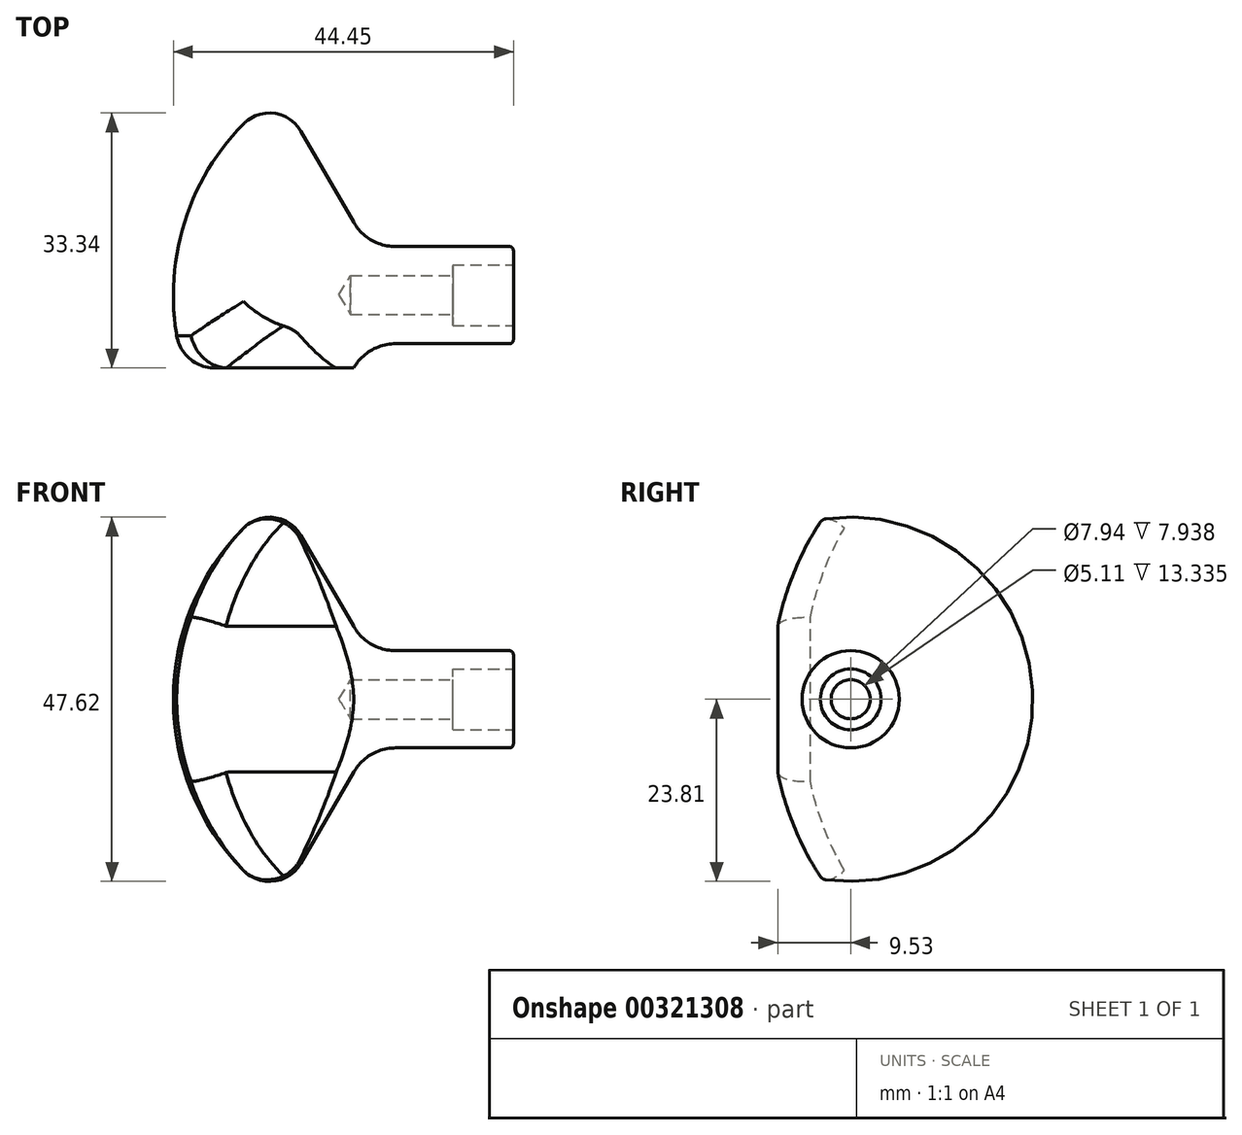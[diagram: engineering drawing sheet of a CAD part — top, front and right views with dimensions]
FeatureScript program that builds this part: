
annotation { "Feature Type Name" : "Feature", "Feature Type Description" : "" }
export const myFeature = defineFeature(function(context is Context, id is Id, definition is map)
    precondition{}
    {
        {
            var Q0;
            Q0=qCreatedBy(makeId("Top.planeOp"),FACE);
            var sketch = newSketch(context, id + "F0", { "sketchPlane" : qUnion([Q0])});
            skLineSegment(sketch, "E0", {"start": v(0, 0) * mm, "end": v(-44.45, 0) * mm});
            skLineSegment(sketch, "E1", {"start": v(0, 0) * mm, "end": v(0, 6.35) * mm});
            skLineSegment(sketch, "E2", {"start": v(0, 6.35) * mm, "end": v(-19.05, 6.35) * mm});
            skLineSegment(sketch, "E3", {"start": v(-19.05, 6.35) * mm, "end": v(-27.76, 21.43) * mm});
            skArc(sketch, "E4", {"start": v(-27.76, 21.43) * mm, "mid": v(-31.28, 23.77) * mm, "end": v(-35.27, 22.4) * mm});
            skLineSegment(sketch, "E5", {"start": v(0, 0) * mm, "end": v(5.66, 0) * mm, "construction": true});
            skArc(sketch, "E6", {"start": v(-35.27, 22.4) * mm, "mid": v(-42.07, 12.1) * mm, "end": v(-44.45, 0) * mm});
            skSolve(sketch);
        }
        {
            var Q0;
            Q0 = qSketchRegion(id + "F0", true);
            var Q1;
            Q1=sQuery(id+"F0.wireOp",EDGE,"E0");
            revolve(context, id + "F1", {"entities" : qUnion([Q0]), "axis" : qUnion([Q1]), "revolveType" : RevolveType.FULL});
        }
        {
            var Q0;
            Q0=makeQuery(id+"F1.opRevolve","SWEPT_FACE",FACE,{"disambiguationData":[OSD([sQuery(id+"F0.wireOp",EDGE,"E1")])]});
            var sketch = newSketch(context, id + "F2", { "sketchPlane" : qUnion([Q0])});
            skPoint(sketch, "E7.middle", {"position": v(0, 0) * mm});
            skLineSegment(sketch, "E8", {"start": v(0, 25.4) * mm, "end": v(0, -25.4) * mm, "construction": true});
            skArc(sketch, "E9", {"start": v(-2.39, 25.4) * mm, "mid": v(-6.87, 17.88) * mm, "end": v(-9.53, 9.53) * mm});
            skLineSegment(sketch, "E10.bottom", {"start": v(-25.4, 25.4) * mm, "end": v(25.4, 25.4) * mm});
            skLineSegment(sketch, "E10.top", {"start": v(-25.4, -25.4) * mm, "end": v(25.4, -25.4) * mm});
            skLineSegment(sketch, "E10.left", {"start": v(-25.4, 25.4) * mm, "end": v(-25.4, -25.4) * mm});
            skLineSegment(sketch, "E10.right", {"start": v(25.4, 25.4) * mm, "end": v(25.4, -25.4) * mm});
            skLineSegment(sketch, "E11", {"start": v(-25.4, 0) * mm, "end": v(25.4, 0) * mm, "construction": true});
            skLineSegment(sketch, "E12", {"start": v(-9.53, 9.53) * mm, "end": v(-9.53, -9.53) * mm});
            skArc(sketch, "E13.MirrorCS", {"start": v(-2.39, -25.4) * mm, "mid": v(-6.87, -17.88) * mm, "end": v(-9.53, -9.53) * mm});
            skSolve(sketch);
        }
        {
            var Q0;
            {var subQ0=sQuery(id+"F2.wireOp",EDGE,"E9");Q0=makeQuery(id+"F2.imprint","IMPRINT",FACE,{"disambiguationData":[TD([[makeQuery(id+"F2.imprint","IMPRINT",EDGE,{"derivedFrom":subQ0}),-1.0]])]});}
            extrude(context, id + "F3", {"entities" : qUnion([Q0]), "operationType" : NewBodyOperationType.REMOVE, "endBound" : BoundingType.THROUGH_ALL, "oppositeDirection" : true, "depth" : 25.4 * mm});
        }
        {
            var Q0;
            Q0=makeQuery(id+"F1.opRevolve","SWEPT_EDGE",EDGE,{"disambiguationData":[OSD([sQuery(id+"F0.wireOp",EDGE,"E2"),sQuery(id+"F0.wireOp",EDGE,"E3")])]});
            fillet(context, id + "F4", {"entities" : qUnion([Q0]), "radius" : 6.35 * mm, "tangentPropagation" : true, "allowEdgeOverflow" : false});
        }
        {
            var Q0;
            Q0=makeQuery(id+"F3.boolean.opBoolean","INTERSECT",EDGE,{"derivedFrom":[makeQuery(id+"F1.opRevolve","SWEPT_FACE",FACE,{"disambiguationData":[OSD([sQuery(id+"F0.wireOp",EDGE,"E6")])]}),makeQuery(id+"F3.opExtrude","SWEPT_FACE",FACE,{"disambiguationData":[OSD([sQuery(id+"F2.wireOp",EDGE,"E12")])]})]});
            var Q1;
            Q1=makeQuery(id+"FgzYNpBnf1yekk4_1.1.F3.boolean.opBoolean","INTERSECT",EDGE,{"derivedFrom":[makeQuery(id+"F1.opRevolve","SWEPT_FACE",FACE,{"disambiguationData":[OSD([sQuery(id+"F0.wireOp",EDGE,"E6")])]}),makeQuery(id+"FgzYNpBnf1yekk4_1.1.F3.opExtrude","SWEPT_FACE",FACE,{"disambiguationData":[OSD([sQuery(id+"F2.wireOp",EDGE,"E12")])]})]});
            fillet(context, id + "F5", {"entities" : qUnion([Q0, Q1]), "radius" : 5.08 * mm, "tangentPropagation" : true, "allowEdgeOverflow" : false});
        }
        {
            var Q0;
            Q0=makeQuery(id+"F1.opRevolve","SWEPT_FACE",FACE,{"disambiguationData":[OSD([sQuery(id+"F0.wireOp",EDGE,"E1")])]});
            var sketch = newSketch(context, id + "F6", { "sketchPlane" : qUnion([Q0])});
            skPoint(sketch, "E14", {"position": v(0, 0) * mm});
            skSolve(sketch);
        }
        {
            var Q0;
            Q0=sQuery(id+"F6.wireOp",VERTEX,"E14");
            var Q1;
            Q1=makeQuery(id+"F1.opRevolve","SWEPT_BODY",BODY,{"disambiguationData":[OSD([sQuery(id+"F0.wireOp",EDGE,"E0"),sQuery(id+"F0.wireOp",EDGE,"MxpznwVz-epMV-FvkS-8xI1-KMkaK6EqJ573"),sQuery(id+"F0.wireOp",EDGE,"E1"),sQuery(id+"F0.wireOp",EDGE,"E2"),sQuery(id+"F0.wireOp",EDGE,"E3"),sQuery(id+"F0.wireOp",EDGE,"J6ywR1Q0-5YNX-wB57-A6pp-HkRRnlB98nbH"),sQuery(id+"F0.wireOp",EDGE,"E4")])]});
            hole(context, id + "F7", {"style" : HoleStyle.SIMPLE, "endStyle" : HoleEndStyle.BLIND, "standardTappedOrClearance" : lookupTablePath({ "standard" : "ANSI", "engagement" : "75%", "pitch" : "20 tpi", "size" : "1/4", "type" : "Tapped" }), "standardBlindInLast" : lookupTablePath({ "standard" : "ANSI", "fit" : "Normal", "engagement" : "75%", "pitch" : "20 tpi", "size" : "1/4", "type" : "Clearance & tapped" }), "holeDiameter" : 5.1 * mm, "majorDiameter" : 6.35 * mm, "showTappedDepth" : true, "holeDepth" : 21.27 * mm, "tappedDepth" : 17.46 * mm, "tapClearance" : 3, "startFromSketch" : true, "locations" : qUnion([Q0]), "scope" : qUnion([Q1])});
        }
        {
            var Q0;
            Q0=makeQuery(id+"F1.opRevolve","SWEPT_FACE",FACE,{"disambiguationData":[OSD([sQuery(id+"F0.wireOp",EDGE,"E1")])]});
            var sketch = newSketch(context, id + "F8", { "sketchPlane" : qUnion([Q0])});
            skCircle(sketch, "E15", {"center": v(0, 0) * mm, "radius": 3.97 * mm});
            skSolve(sketch);
        }
        {
            var Q0;
            Q0 = qSketchRegion(id + "F8", true);
            extrude(context, id + "F9", {"entities" : qUnion([Q0]), "operationType" : NewBodyOperationType.REMOVE, "oppositeDirection" : true, "depth" : 7.94 * mm, "offsetDistance" : 25.4 * mm});
        }
        {
            var Q0;
            Q0=makeQuery(id+"F1.opRevolve","SWEPT_EDGE",EDGE,{"disambiguationData":[OSD([sQuery(id+"F0.wireOp",EDGE,"E1"),sQuery(id+"F0.wireOp",EDGE,"E2")])]});
            fillet(context, id + "F10", {"entities" : qUnion([Q0]), "radius" : 0.5 * mm, "tangentPropagation" : true, "allowEdgeOverflow" : false});
        }
        {
            var Q0;
            Q0=makeQuery(id+"FgzYNpBnf1yekk4_1.1.F3.boolean.opBoolean","INTERSECT",EDGE,{"derivedFrom":[makeQuery(id+"F1.opRevolve","SWEPT_FACE",FACE,{"disambiguationData":[OSD([sQuery(id+"F0.wireOp",EDGE,"E6")])]}),makeQuery(id+"FgzYNpBnf1yekk4_1.1.F3.opExtrude","SWEPT_FACE",FACE,{"disambiguationData":[OSD([sQuery(id+"F2.wireOp",EDGE,"E9")])]})]});
            var Q1;
            Q1=makeQuery(id+"F3.boolean.opBoolean","INTERSECT",EDGE,{"derivedFrom":[makeQuery(id+"F1.opRevolve","SWEPT_FACE",FACE,{"disambiguationData":[OSD([sQuery(id+"F0.wireOp",EDGE,"E6")])]}),makeQuery(id+"F3.opExtrude","SWEPT_FACE",FACE,{"disambiguationData":[OSD([sQuery(id+"F2.wireOp",EDGE,"E9")])]})]});
            var Q2;
            Q2=makeQuery(id+"F3.boolean.opBoolean","INTERSECT",EDGE,{"derivedFrom":[makeQuery(id+"F1.opRevolve","SWEPT_FACE",FACE,{"disambiguationData":[OSD([sQuery(id+"F0.wireOp",EDGE,"E6")])]}),makeQuery(id+"F3.opExtrude","SWEPT_FACE",FACE,{"disambiguationData":[OSD([sQuery(id+"F2.wireOp",EDGE,"E13.MirrorCS")])]})]});
            var Q3;
            Q3=makeQuery(id+"FgzYNpBnf1yekk4_1.1.F3.boolean.opBoolean","INTERSECT",EDGE,{"derivedFrom":[makeQuery(id+"F1.opRevolve","SWEPT_FACE",FACE,{"disambiguationData":[OSD([sQuery(id+"F0.wireOp",EDGE,"E6")])]}),makeQuery(id+"FgzYNpBnf1yekk4_1.1.F3.opExtrude","SWEPT_FACE",FACE,{"disambiguationData":[OSD([sQuery(id+"F2.wireOp",EDGE,"E13.MirrorCS")])]})]});
            fillet(context, id + "F11", {"entities" : qUnion([Q0, Q1, Q2, Q3]), "radius" : 5.08 * mm, "allowEdgeOverflow" : false});
        }
    });
